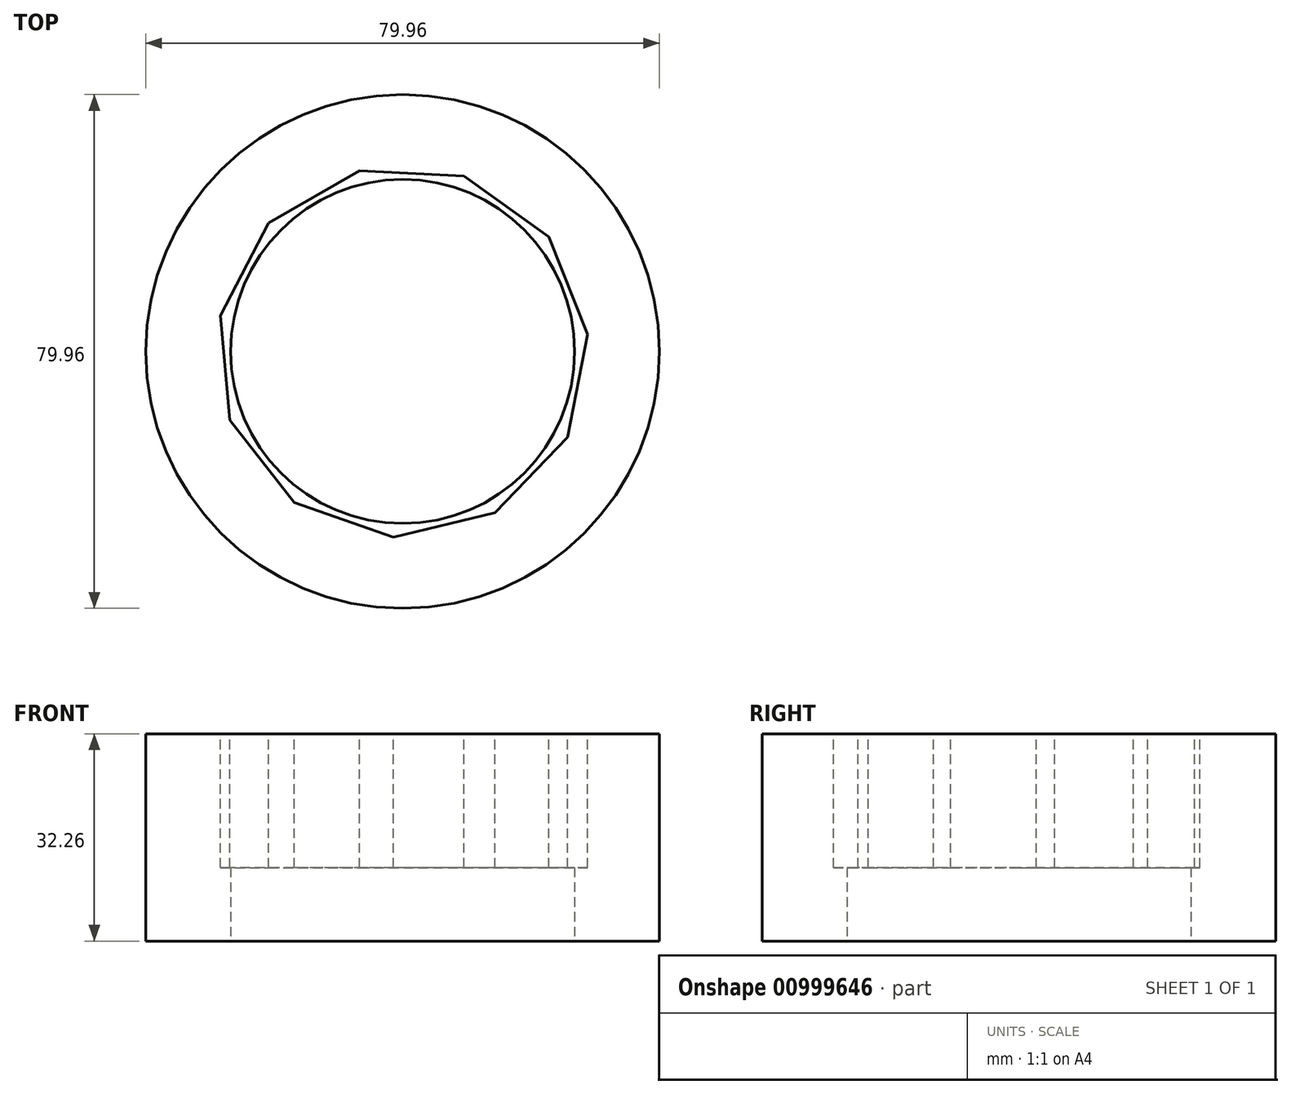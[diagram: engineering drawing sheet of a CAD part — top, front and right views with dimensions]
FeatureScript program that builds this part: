
annotation { "Feature Type Name" : "Feature", "Feature Type Description" : "" }
export const myFeature = defineFeature(function(context is Context, id is Id, definition is map)
    precondition{}
    {
        {
            var Q0;
            Q0=qCreatedBy(makeId("Top.planeOp"),FACE);
            var sketch = newSketch(context, id + "F0", { "sketchPlane" : qUnion([Q0])});
            skCircle(sketch, "E0", {"center": v(0, 0) * mm, "radius": 39.98 * mm});
            skSolve(sketch);
        }
        {
            var Q0;
            Q0=makeQuery(id+"F0.imprint","IMPRINT",FACE,{"disambiguationData":[TD([[makeQuery(id+"F0.imprint","IMPRINT",EDGE,{"derivedFrom":sQuery(id+"F0.wireOp",EDGE,"E0")}),1.0]])]});
            extrude(context, id + "F1", {"entities" : qUnion([Q0]), "depth" : 53.6 * mm, "offsetDistance" : 25.4 * mm});
        }
        {
            var Q0;
            Q0=makeQuery(id+"F1.opExtrude","CAP_FACE",FACE,{"disambiguationData":[OSD([sQuery(id+"F0.wireOp",EDGE,"E0")])],"isStart":false});
            var sketch = newSketch(context, id + "F2", { "sketchPlane" : qUnion([Q0])});
            skCircle(sketch, "E1.cCircle", {"center": v(0, 0) * mm, "radius": 27.74 * mm, "construction": true});
            skLineSegment(sketch, "E1.0", {"start": v(14.39, -25.08) * mm, "end": v(-1.46, -28.88) * mm});
            skLineSegment(sketch, "E1.1", {"start": v(-1.46, -28.88) * mm, "end": v(-16.84, -23.5) * mm});
            skLineSegment(sketch, "E1.2", {"start": v(-16.84, -23.5) * mm, "end": v(-26.87, -10.67) * mm});
            skLineSegment(sketch, "E1.3", {"start": v(-26.87, -10.67) * mm, "end": v(-28.37, 5.55) * mm});
            skLineSegment(sketch, "E1.4", {"start": v(-28.37, 5.55) * mm, "end": v(-20.87, 20.01) * mm});
            skLineSegment(sketch, "E1.5", {"start": v(-20.87, 20.01) * mm, "end": v(-6.74, 28.12) * mm});
            skLineSegment(sketch, "E1.6", {"start": v(-6.74, 28.12) * mm, "end": v(9.53, 27.3) * mm});
            skLineSegment(sketch, "E1.7", {"start": v(9.53, 27.3) * mm, "end": v(22.78, 17.8) * mm});
            skLineSegment(sketch, "E1.8", {"start": v(22.78, 17.8) * mm, "end": v(28.79, 2.67) * mm});
            skLineSegment(sketch, "E1.9", {"start": v(28.79, 2.67) * mm, "end": v(25.66, -13.32) * mm});
            skLineSegment(sketch, "E1.10", {"start": v(25.66, -13.32) * mm, "end": v(14.39, -25.08) * mm});
            skPoint(sketch, "E1.0.midPoint", {"position": v(6.46, -26.98) * mm});
            skSolve(sketch);
        }
        {
            var Q0;
            Q0=makeQuery(id+"F2.imprint","IMPRINT",FACE,{"disambiguationData":[TD([[makeQuery(id+"F2.imprint","IMPRINT",EDGE,{"derivedFrom":sQuery(id+"F2.wireOp",EDGE,"E1.0")}),-1.0]])]});
            extrude(context, id + "F3", {"entities" : qUnion([Q0]), "operationType" : NewBodyOperationType.ADD, "depth" : 24.64 * mm, "offsetDistance" : 25.4 * mm});
        }
        {
            var Q0;
            Q0=makeQuery(id+"F3.opExtrude","CAP_FACE",FACE,{"disambiguationData":[OSD([sQuery(id+"F2.wireOp",EDGE,"E1.0"),sQuery(id+"F2.wireOp",EDGE,"E1.1"),sQuery(id+"F2.wireOp",EDGE,"E1.2"),sQuery(id+"F2.wireOp",EDGE,"E1.3"),sQuery(id+"F2.wireOp",EDGE,"E1.4"),sQuery(id+"F2.wireOp",EDGE,"E1.5"),sQuery(id+"F2.wireOp",EDGE,"E1.6"),sQuery(id+"F2.wireOp",EDGE,"E1.7"),sQuery(id+"F2.wireOp",EDGE,"E1.8"),sQuery(id+"F2.wireOp",EDGE,"E1.9"),sQuery(id+"F2.wireOp",EDGE,"E1.10")])],"isStart":false});
            extrude(context, id + "F4", {"entities" : qUnion([Q0]), "operationType" : NewBodyOperationType.REMOVE, "oppositeDirection" : true, "depth" : 66.8 * mm, "offsetDistance" : 25.4 * mm});
        }
        {
            var Q0;
            Q0=makeQuery(id+"F1.opExtrude","CAP_FACE",FACE,{"disambiguationData":[OSD([sQuery(id+"F0.wireOp",EDGE,"E0")])],"isStart":true});
            var sketch = newSketch(context, id + "F5", { "sketchPlane" : qUnion([Q0])});
            skCircle(sketch, "E2.0", {"center": v(0, 0) * mm, "radius": 26.77 * mm});
            skSolve(sketch);
        }
        {
            var Q0;
            Q0=makeQuery(id+"F5.imprint","IMPRINT",FACE,{"disambiguationData":[TD([[makeQuery(id+"F5.imprint","IMPRINT",EDGE,{"derivedFrom":sQuery(id+"F5.wireOp",EDGE,"E2.0")}),1.0]])]});
            extrude(context, id + "F6", {"entities" : qUnion([Q0]), "operationType" : NewBodyOperationType.REMOVE, "oppositeDirection" : true, "depth" : 37.6 * mm, "offsetDistance" : 25.4 * mm});
        }
        {
            var Q0;
            Q0=makeQuery(id+"F1.opExtrude","CAP_FACE",FACE,{"disambiguationData":[OSD([sQuery(id+"F0.wireOp",EDGE,"E0")])],"isStart":false});
            extrude(context, id + "F7", {"entities" : qUnion([Q0]), "operationType" : NewBodyOperationType.REMOVE, "oppositeDirection" : true, "depth" : 21.34 * mm, "offsetDistance" : 25.4 * mm});
        }
    });
